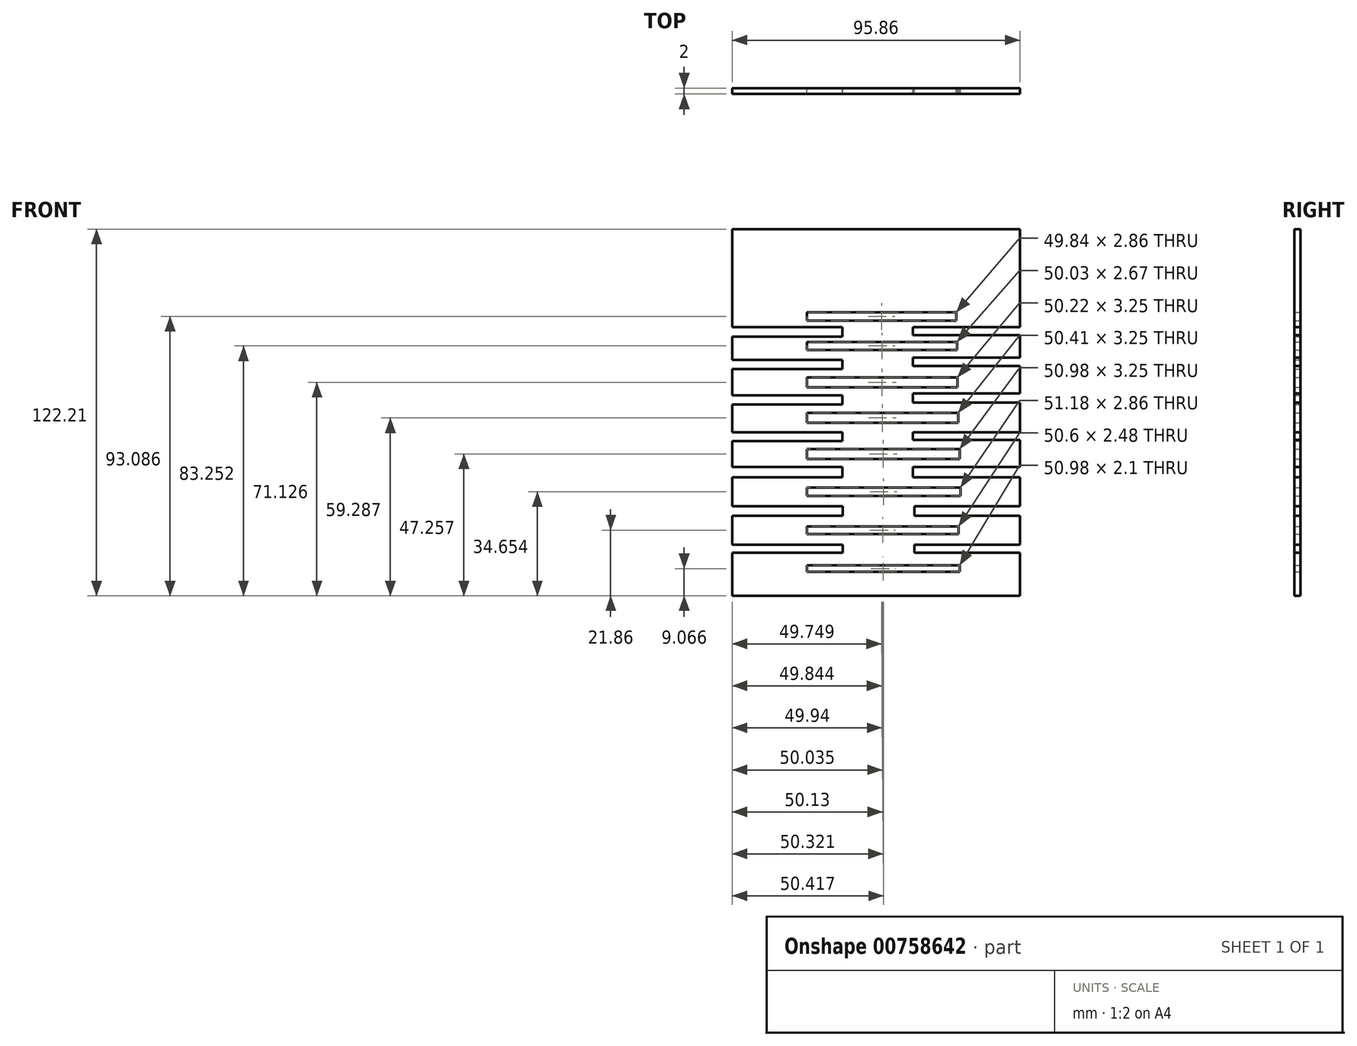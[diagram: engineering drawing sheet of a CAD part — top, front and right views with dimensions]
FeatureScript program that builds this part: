
annotation { "Feature Type Name" : "Feature", "Feature Type Description" : "" }
export const myFeature = defineFeature(function(context is Context, id is Id, definition is map)
    precondition{}
    {
        {
            var Q0;
            Q0=qCreatedBy(makeId("Front.planeOp"),FACE);
            var sketch = newSketch(context, id + "F0", { "sketchPlane" : qUnion([Q0])});
            skLineSegment(sketch, "E0.bottom", {"start": v(-48.03, -55.85) * mm, "end": v(47.83, -55.85) * mm});
            skLineSegment(sketch, "E0.top", {"start": v(-48.03, 66.36) * mm, "end": v(47.83, 66.36) * mm});
            skLineSegment(sketch, "E0.left", {"start": v(-48.03, -55.85) * mm, "end": v(-48.03, -41.53) * mm});
            skLineSegment(sketch, "E0.right", {"start": v(47.83, -55.85) * mm, "end": v(47.83, -41.53) * mm});
            skLineSegment(sketch, "E1.bottom", {"start": v(-23.2, -47.83) * mm, "end": v(27.78, -47.83) * mm});
            skLineSegment(sketch, "E1.top", {"start": v(-23.2, -45.73) * mm, "end": v(27.78, -45.73) * mm});
            skLineSegment(sketch, "E1.left", {"start": v(-23.2, -47.83) * mm, "end": v(-23.2, -45.73) * mm});
            skLineSegment(sketch, "E1.right", {"start": v(27.78, -47.83) * mm, "end": v(27.78, -45.73) * mm});
            skLineSegment(sketch, "E2.bottom", {"start": v(-48.03, -41.53) * mm, "end": v(-11.17, -41.53) * mm});
            skLineSegment(sketch, "E2.top", {"start": v(-48.03, -38.86) * mm, "end": v(-11.17, -38.86) * mm});
            skLineSegment(sketch, "E2.right", {"start": v(-11.17, -41.53) * mm, "end": v(-11.17, -38.86) * mm});
            skLineSegment(sketch, "E3.bottom", {"start": v(47.83, -38.86) * mm, "end": v(12.7, -38.86) * mm});
            skLineSegment(sketch, "E3.top", {"start": v(47.83, -41.53) * mm, "end": v(12.7, -41.53) * mm});
            skLineSegment(sketch, "E3.right", {"start": v(12.7, -38.86) * mm, "end": v(12.7, -41.53) * mm});
            skLineSegment(sketch, "E4.trimOffspring", {"start": v(47.83, -38.86) * mm, "end": v(47.83, -29.12) * mm});
            skLineSegment(sketch, "E5.trimOffspring", {"start": v(-48.03, -38.86) * mm, "end": v(-48.03, -29.12) * mm});
            skLineSegment(sketch, "E6.bottom", {"start": v(-23.2, -35.23) * mm, "end": v(27.4, -35.23) * mm});
            skLineSegment(sketch, "E6.top", {"start": v(-23.2, -32.75) * mm, "end": v(27.4, -32.75) * mm});
            skLineSegment(sketch, "E6.left", {"start": v(-23.2, -35.23) * mm, "end": v(-23.2, -32.75) * mm});
            skLineSegment(sketch, "E6.right", {"start": v(27.4, -35.23) * mm, "end": v(27.4, -32.75) * mm});
            skLineSegment(sketch, "E7.bottom", {"start": v(-11.17, -29.12) * mm, "end": v(-48.03, -29.12) * mm});
            skLineSegment(sketch, "E7.top", {"start": v(-11.17, -26.07) * mm, "end": v(-48.03, -26.07) * mm});
            skLineSegment(sketch, "E7.left", {"start": v(-11.17, -29.12) * mm, "end": v(-11.17, -26.07) * mm});
            skLineSegment(sketch, "E8.bottom", {"start": v(12.7, -29.12) * mm, "end": v(47.83, -29.12) * mm});
            skLineSegment(sketch, "E8.top", {"start": v(12.7, -26.07) * mm, "end": v(47.83, -26.07) * mm});
            skLineSegment(sketch, "E8.left", {"start": v(12.7, -29.12) * mm, "end": v(12.7, -26.07) * mm});
            skLineSegment(sketch, "E9.trimOffspring", {"start": v(47.83, -26.07) * mm, "end": v(47.83, -16.33) * mm});
            skLineSegment(sketch, "E10.trimOffspring", {"start": v(-48.03, -26.07) * mm, "end": v(-48.03, -16.33) * mm});
            skLineSegment(sketch, "E11.bottom", {"start": v(-23.2, -22.63) * mm, "end": v(27.97, -22.63) * mm});
            skLineSegment(sketch, "E11.top", {"start": v(-23.2, -19.76) * mm, "end": v(27.97, -19.76) * mm});
            skLineSegment(sketch, "E11.left", {"start": v(-23.2, -22.63) * mm, "end": v(-23.2, -19.76) * mm});
            skLineSegment(sketch, "E11.right", {"start": v(27.97, -22.63) * mm, "end": v(27.97, -19.76) * mm});
            skLineSegment(sketch, "E12.bottom", {"start": v(-11.36, -16.33) * mm, "end": v(-48.03, -16.33) * mm});
            skLineSegment(sketch, "E12.top", {"start": v(-11.36, -12.89) * mm, "end": v(-48.03, -12.89) * mm});
            skLineSegment(sketch, "E12.left", {"start": v(-11.36, -16.33) * mm, "end": v(-11.36, -12.89) * mm});
            skLineSegment(sketch, "E13.trimOffspring", {"start": v(-48.03, -12.89) * mm, "end": v(-48.03, -4.3) * mm});
            skLineSegment(sketch, "E14.bottom", {"start": v(12.13, -16.33) * mm, "end": v(47.83, -16.33) * mm});
            skLineSegment(sketch, "E14.top", {"start": v(12.13, -12.89) * mm, "end": v(47.83, -12.89) * mm});
            skLineSegment(sketch, "E14.left", {"start": v(12.13, -16.33) * mm, "end": v(12.13, -12.89) * mm});
            skLineSegment(sketch, "E15.trimOffspring", {"start": v(47.83, -12.89) * mm, "end": v(47.83, -3.91) * mm});
            skLineSegment(sketch, "E16.bottom", {"start": v(-23.2, -10.22) * mm, "end": v(27.78, -10.22) * mm});
            skLineSegment(sketch, "E16.top", {"start": v(-23.2, -6.97) * mm, "end": v(27.78, -6.97) * mm});
            skLineSegment(sketch, "E16.left", {"start": v(-23.2, -10.22) * mm, "end": v(-23.2, -6.97) * mm});
            skLineSegment(sketch, "E16.right", {"start": v(27.78, -10.22) * mm, "end": v(27.78, -6.97) * mm});
            skLineSegment(sketch, "E17.bottom", {"start": v(-11.36, -4.3) * mm, "end": v(-48.03, -4.3) * mm});
            skLineSegment(sketch, "E17.top", {"start": v(-11.36, -1.43) * mm, "end": v(-48.03, -1.43) * mm});
            skLineSegment(sketch, "E17.left", {"start": v(-11.36, -4.3) * mm, "end": v(-11.36, -1.43) * mm});
            skLineSegment(sketch, "E18.trimOffspring", {"start": v(-48.03, -1.43) * mm, "end": v(-48.03, 7.92) * mm});
            skLineSegment(sketch, "E19.bottom", {"start": v(12.13, -3.91) * mm, "end": v(47.83, -3.91) * mm});
            skLineSegment(sketch, "E19.top", {"start": v(12.13, -1.43) * mm, "end": v(47.83, -1.43) * mm});
            skLineSegment(sketch, "E19.left", {"start": v(12.13, -3.91) * mm, "end": v(12.13, -1.43) * mm});
            skLineSegment(sketch, "E20.trimOffspring", {"start": v(47.83, -1.43) * mm, "end": v(47.83, 8.5) * mm});
            skLineSegment(sketch, "E21.bottom", {"start": v(-23.2, 1.81) * mm, "end": v(27.21, 1.81) * mm});
            skLineSegment(sketch, "E21.top", {"start": v(-23.2, 5.06) * mm, "end": v(27.21, 5.06) * mm});
            skLineSegment(sketch, "E21.left", {"start": v(-23.2, 1.81) * mm, "end": v(-23.2, 5.06) * mm});
            skLineSegment(sketch, "E21.right", {"start": v(27.21, 1.81) * mm, "end": v(27.21, 5.06) * mm});
            skLineSegment(sketch, "E22.bottom", {"start": v(-11.36, 7.92) * mm, "end": v(-48.03, 7.92) * mm});
            skLineSegment(sketch, "E22.top", {"start": v(-11.36, 10.98) * mm, "end": v(-48.03, 10.98) * mm});
            skLineSegment(sketch, "E22.left", {"start": v(-11.36, 7.92) * mm, "end": v(-11.36, 10.98) * mm});
            skLineSegment(sketch, "E23.bottom", {"start": v(12.13, 8.5) * mm, "end": v(47.83, 8.5) * mm});
            skLineSegment(sketch, "E23.top", {"start": v(12.13, 11.55) * mm, "end": v(47.83, 11.55) * mm});
            skLineSegment(sketch, "E23.left", {"start": v(12.13, 8.5) * mm, "end": v(12.13, 11.55) * mm});
            skLineSegment(sketch, "E24.trimOffspring", {"start": v(-48.03, 10.98) * mm, "end": v(-48.03, 19.76) * mm});
            skLineSegment(sketch, "E25.trimOffspring", {"start": v(47.83, 11.55) * mm, "end": v(47.83, 20.72) * mm});
            skLineSegment(sketch, "E26.bottom", {"start": v(-23.2, 13.65) * mm, "end": v(27.02, 13.65) * mm});
            skLineSegment(sketch, "E26.top", {"start": v(-23.2, 16.9) * mm, "end": v(27.02, 16.9) * mm});
            skLineSegment(sketch, "E26.left", {"start": v(-23.2, 13.65) * mm, "end": v(-23.2, 16.9) * mm});
            skLineSegment(sketch, "E26.right", {"start": v(27.02, 13.65) * mm, "end": v(27.02, 16.9) * mm});
            skLineSegment(sketch, "E27.bottom", {"start": v(-11.36, 19.76) * mm, "end": v(-48.03, 19.76) * mm});
            skLineSegment(sketch, "E27.top", {"start": v(-11.36, 22.82) * mm, "end": v(-48.03, 22.82) * mm});
            skLineSegment(sketch, "E27.left", {"start": v(-11.36, 19.76) * mm, "end": v(-11.36, 22.82) * mm});
            skLineSegment(sketch, "E28.bottom", {"start": v(12.13, 20.72) * mm, "end": v(47.83, 20.72) * mm});
            skLineSegment(sketch, "E28.top", {"start": v(12.13, 23.58) * mm, "end": v(47.83, 23.58) * mm});
            skLineSegment(sketch, "E28.left", {"start": v(12.13, 20.72) * mm, "end": v(12.13, 23.58) * mm});
            skLineSegment(sketch, "E29.trimOffspring", {"start": v(47.83, 23.58) * mm, "end": v(47.83, 31.03) * mm});
            skLineSegment(sketch, "E30.trimOffspring", {"start": v(-48.03, 22.82) * mm, "end": v(-48.03, 30.46) * mm});
            skLineSegment(sketch, "E31.bottom", {"start": v(-23.2, 26.07) * mm, "end": v(26.83, 26.07) * mm});
            skLineSegment(sketch, "E31.top", {"start": v(-23.2, 28.74) * mm, "end": v(26.83, 28.74) * mm});
            skLineSegment(sketch, "E31.left", {"start": v(-23.2, 26.07) * mm, "end": v(-23.2, 28.74) * mm});
            skLineSegment(sketch, "E31.right", {"start": v(26.83, 26.07) * mm, "end": v(26.83, 28.74) * mm});
            skLineSegment(sketch, "E32.bottom", {"start": v(12.13, 31.03) * mm, "end": v(47.83, 31.03) * mm});
            skLineSegment(sketch, "E32.top", {"start": v(12.13, 33.7) * mm, "end": v(47.83, 33.7) * mm});
            skLineSegment(sketch, "E32.left", {"start": v(12.13, 31.03) * mm, "end": v(12.13, 33.7) * mm});
            skLineSegment(sketch, "E33.bottom", {"start": v(-11.36, 30.46) * mm, "end": v(-48.03, 30.46) * mm});
            skLineSegment(sketch, "E33.top", {"start": v(-11.36, 33.7) * mm, "end": v(-48.03, 33.7) * mm});
            skLineSegment(sketch, "E33.left", {"start": v(-11.36, 30.46) * mm, "end": v(-11.36, 33.7) * mm});
            skLineSegment(sketch, "E34.bottom", {"start": v(-23.2, 35.8) * mm, "end": v(26.64, 35.8) * mm});
            skLineSegment(sketch, "E34.top", {"start": v(-23.2, 38.67) * mm, "end": v(26.64, 38.67) * mm});
            skLineSegment(sketch, "E34.left", {"start": v(-23.2, 35.8) * mm, "end": v(-23.2, 38.67) * mm});
            skLineSegment(sketch, "E34.right", {"start": v(26.64, 35.8) * mm, "end": v(26.64, 38.67) * mm});
            skLineSegment(sketch, "E35.trimOffspring", {"start": v(-48.03, 33.7) * mm, "end": v(-48.03, 66.36) * mm});
            skLineSegment(sketch, "E36.trimOffspring", {"start": v(47.83, 33.7) * mm, "end": v(47.83, 66.36) * mm});
            skSolve(sketch);
        }
        {
            var Q0;
            Q0=qSketchRegion(id+"F0",true);
            extrude(context, id + "F1", {"entities" : qUnion([Q0]), "depth" : 2 * mm, "offsetDistance" : 25.4 * mm});
        }
    });
